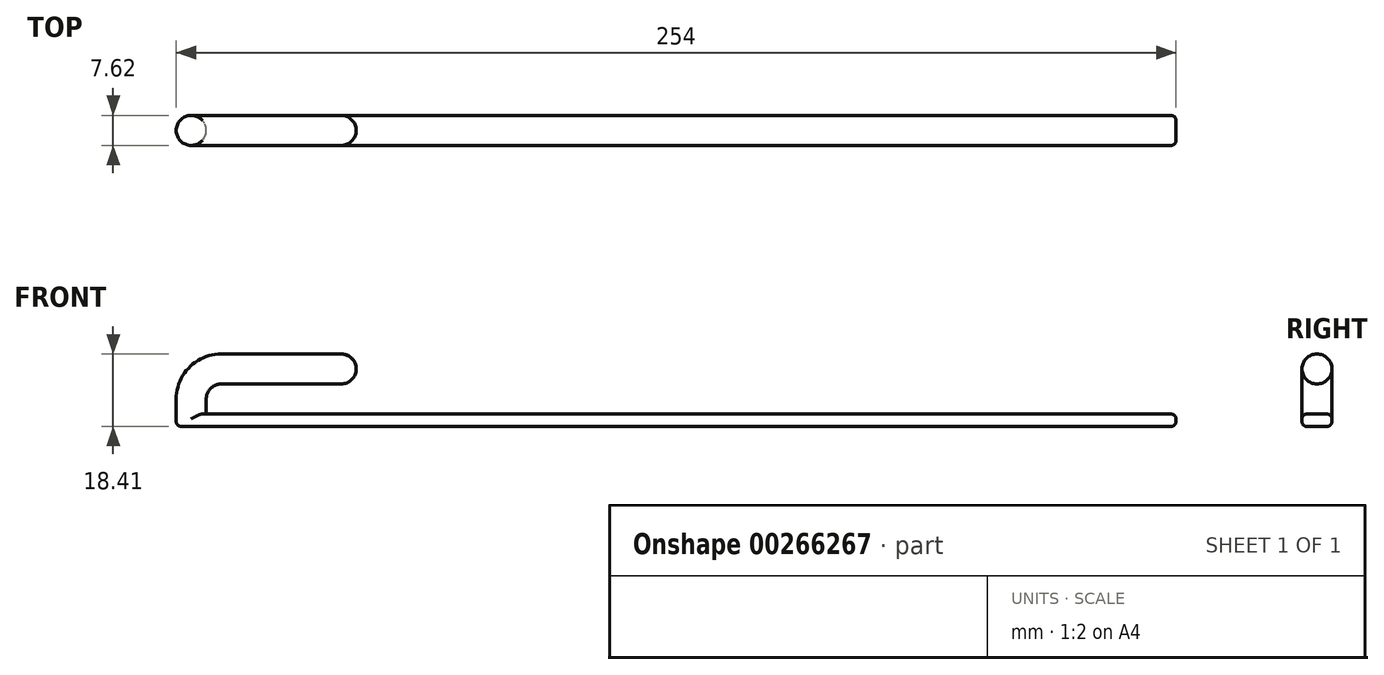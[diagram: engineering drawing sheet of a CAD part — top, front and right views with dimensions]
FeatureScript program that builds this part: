
annotation { "Feature Type Name" : "Feature", "Feature Type Description" : "" }
export const myFeature = defineFeature(function(context is Context, id is Id, definition is map)
    precondition{}
    {
        {
            var Q0;
            Q0=qCreatedBy(makeId("Front.planeOp"),FACE);
            var sketch = newSketch(context, id + "F0", { "sketchPlane" : qUnion([Q0])});
            skLineSegment(sketch, "E0.bottom", {"start": v(-111.6, 37.2) * mm, "end": v(134.77, 37.2) * mm});
            skLineSegment(sketch, "E0.top", {"start": v(-119.23, 34.03) * mm, "end": v(134.77, 34.03) * mm});
            skLineSegment(sketch, "E0.left", {"start": v(-119.23, 39.1) * mm, "end": v(-119.23, 37.2) * mm});
            skLineSegment(sketch, "E0.right", {"start": v(134.77, 37.2) * mm, "end": v(134.77, 34.03) * mm});
            skLineSegment(sketch, "E1.left", {"start": v(-119.23, 34.03) * mm, "end": v(-119.23, 44.82) * mm});
            skLineSegment(sketch, "E1.right", {"start": v(-111.6, 37.2) * mm, "end": v(-111.6, 41.01) * mm});
            skLineSegment(sketch, "E2.bottom", {"start": v(-107.8, 44.82) * mm, "end": v(-73.5, 44.82) * mm});
            skLineSegment(sketch, "E2.top", {"start": v(-107.8, 52.44) * mm, "end": v(-73.5, 52.44) * mm});
            skLineSegment(sketch, "E2.left", {"start": v(-119.23, 41.01) * mm, "end": v(-119.23, 44.82) * mm});
            skLineSegment(sketch, "E2.right", {"start": v(-73.5, 44.82) * mm, "end": v(-73.5, 52.44) * mm});
            skPoint(sketch, "E3.visualSharp", {"position": v(-119.23, 52.44) * mm});
            skArc(sketch, "E3.filletArc", {"start": v(-107.8, 52.44) * mm, "mid": v(-115.88, 49.1) * mm, "end": v(-119.23, 41.01) * mm});
            skPoint(sketch, "E4.visualSharp", {"position": v(-111.6, 44.82) * mm});
            skArc(sketch, "E4.filletArc", {"start": v(-107.8, 44.82) * mm, "mid": v(-110.5, 43.7) * mm, "end": v(-111.6, 41.01) * mm});
            skPoint(sketch, "E5.visualSharp", {"position": v(-111.6, 37.2) * mm});
            skPoint(sketch, "E6.visualSharp", {"position": v(-119.23, 34.03) * mm});
            skSolve(sketch);
        }
        {
            var Q0;
            Q0=makeQuery(id+"F0.imprint","IMPRINT",FACE,{"disambiguationData":[TD([[makeQuery(id+"F0.imprint","IMPRINT",EDGE,{"derivedFrom":sQuery(id+"F0.wireOp",EDGE,"E0.bottom")}),-1.0]])]});
            extrude(context, id + "F1", {"entities" : qUnion([Q0]), "depth" : 7.62 * mm});
        }
        {
            var Q0;
            Q0=makeQuery(id+"F1.opExtrude","CAP_EDGE",EDGE,{"disambiguationData":[OSD([sQuery(id+"F0.wireOp",EDGE,"E2.top")])],"isStart":false});
            var Q1;
            Q1=makeQuery(id+"F1.opExtrude","CAP_EDGE",EDGE,{"disambiguationData":[OSD([sQuery(id+"F0.wireOp",EDGE,"E2.bottom")])],"isStart":false});
            var Q2;
            Q2=makeQuery(id+"F1.opExtrude","CAP_EDGE",EDGE,{"disambiguationData":[OSD([sQuery(id+"F0.wireOp",EDGE,"E2.bottom")])],"isStart":true});
            var Q3;
            Q3=makeQuery(id+"F1.opExtrude","CAP_EDGE",EDGE,{"disambiguationData":[OSD([sQuery(id+"F0.wireOp",EDGE,"E2.top")])],"isStart":true});
            fillet(context, id + "F2", {"entities" : qUnion([Q0, Q1, Q2, Q3]), "radius" : 3.8 * mm, "tangentPropagation" : true, "allowEdgeOverflow" : false});
        }
        {
            var Q0;
            Q0=makeQuery(id+"F1.opExtrude","SWEPT_EDGE",EDGE,{"disambiguationData":[OSD([sQuery(id+"F0.wireOp",EDGE,"E2.top"),sQuery(id+"F0.wireOp",EDGE,"E2.right")])]});
            var Q1;
            Q1=makeQuery(id+"F2.opFillet","BLEND_EDGE",EDGE,{"blendedFrom":[makeQuery(id+"F1.opExtrude","CAP_EDGE",EDGE,{"disambiguationData":[OSD([sQuery(id+"F0.wireOp",EDGE,"E2.top")])],"isStart":true}),makeQuery(id+"F1.opExtrude","SWEPT_FACE",FACE,{"disambiguationData":[OSD([sQuery(id+"F0.wireOp",EDGE,"E2.right")])]})],"blendedInto":[makeQuery(id+"F1.opExtrude","SWEPT_FACE",FACE,{"disambiguationData":[OSD([sQuery(id+"F0.wireOp",EDGE,"E2.right")])]})]});
            var Q2;
            Q2=makeQuery(id+"F1.opExtrude","CAP_EDGE",EDGE,{"disambiguationData":[OSD([sQuery(id+"F0.wireOp",EDGE,"E2.right")])],"isStart":true});
            var Q3;
            Q3=makeQuery(id+"F2.opFillet","BLEND_EDGE",EDGE,{"blendedFrom":[makeQuery(id+"F1.opExtrude","CAP_EDGE",EDGE,{"disambiguationData":[OSD([sQuery(id+"F0.wireOp",EDGE,"E2.bottom")])],"isStart":true}),makeQuery(id+"F1.opExtrude","SWEPT_FACE",FACE,{"disambiguationData":[OSD([sQuery(id+"F0.wireOp",EDGE,"E2.right")])]})],"blendedInto":[makeQuery(id+"F1.opExtrude","SWEPT_FACE",FACE,{"disambiguationData":[OSD([sQuery(id+"F0.wireOp",EDGE,"E2.right")])]})]});
            var Q4;
            Q4=makeQuery(id+"F1.opExtrude","SWEPT_EDGE",EDGE,{"disambiguationData":[OSD([sQuery(id+"F0.wireOp",EDGE,"E2.bottom"),sQuery(id+"F0.wireOp",EDGE,"E2.right")])]});
            var Q5;
            Q5=makeQuery(id+"F2.opFillet","BLEND_EDGE",EDGE,{"blendedFrom":[makeQuery(id+"F1.opExtrude","CAP_EDGE",EDGE,{"disambiguationData":[OSD([sQuery(id+"F0.wireOp",EDGE,"E2.bottom")])],"isStart":false}),makeQuery(id+"F1.opExtrude","SWEPT_FACE",FACE,{"disambiguationData":[OSD([sQuery(id+"F0.wireOp",EDGE,"E2.right")])]})],"blendedInto":[makeQuery(id+"F1.opExtrude","SWEPT_FACE",FACE,{"disambiguationData":[OSD([sQuery(id+"F0.wireOp",EDGE,"E2.right")])]})]});
            var Q6;
            Q6=makeQuery(id+"F2.opFillet","BLEND_EDGE",EDGE,{"blendedFrom":[makeQuery(id+"F1.opExtrude","CAP_EDGE",EDGE,{"disambiguationData":[OSD([sQuery(id+"F0.wireOp",EDGE,"E2.top")])],"isStart":false}),makeQuery(id+"F1.opExtrude","SWEPT_FACE",FACE,{"disambiguationData":[OSD([sQuery(id+"F0.wireOp",EDGE,"E2.right")])]})],"blendedInto":[makeQuery(id+"F1.opExtrude","SWEPT_FACE",FACE,{"disambiguationData":[OSD([sQuery(id+"F0.wireOp",EDGE,"E2.right")])]})]});
            var Q7;
            Q7=makeQuery(id+"F1.opExtrude","CAP_EDGE",EDGE,{"disambiguationData":[OSD([sQuery(id+"F0.wireOp",EDGE,"E2.right")])],"isStart":false});
            fillet(context, id + "F3", {"entities" : qUnion([Q0, Q1, Q2, Q3, Q4, Q5, Q6, Q7]), "radius" : 3.8 * mm, "tangentPropagation" : true, "allowEdgeOverflow" : false});
        }
        {
            var Q0;
            Q0=makeQuery(id+"F1.opExtrude","CAP_EDGE",EDGE,{"disambiguationData":[OSD([sQuery(id+"F0.wireOp",EDGE,"E0.bottom")])],"isStart":false});
            var Q1;
            Q1=makeQuery(id+"F1.opExtrude","CAP_EDGE",EDGE,{"disambiguationData":[OSD([sQuery(id+"F0.wireOp",EDGE,"E0.top")])],"isStart":false});
            var Q2;
            Q2=makeQuery(id+"F1.opExtrude","CAP_EDGE",EDGE,{"disambiguationData":[OSD([sQuery(id+"F0.wireOp",EDGE,"E0.bottom")])],"isStart":true});
            var Q3;
            Q3=makeQuery(id+"F1.opExtrude","CAP_EDGE",EDGE,{"disambiguationData":[OSD([sQuery(id+"F0.wireOp",EDGE,"E0.top")])],"isStart":true});
            fillet(context, id + "F4", {"entities" : qUnion([Q0, Q1, Q2, Q3]), "radius" : 1.27 * mm, "tangentPropagation" : true, "allowEdgeOverflow" : false});
        }
        {
            var Q0;
            Q0=makeQuery(id+"F4.opFillet","BLEND_EDGE",EDGE,{"blendedFrom":[makeQuery(id+"F1.opExtrude","CAP_EDGE",EDGE,{"disambiguationData":[OSD([sQuery(id+"F0.wireOp",EDGE,"E0.bottom")])],"isStart":false}),makeQuery(id+"F1.opExtrude","SWEPT_FACE",FACE,{"disambiguationData":[OSD([sQuery(id+"F0.wireOp",EDGE,"E0.right")])]})],"blendedInto":[makeQuery(id+"F1.opExtrude","SWEPT_FACE",FACE,{"disambiguationData":[OSD([sQuery(id+"F0.wireOp",EDGE,"E0.right")])]})]});
            var Q1;
            Q1=makeQuery(id+"F1.opExtrude","CAP_EDGE",EDGE,{"disambiguationData":[OSD([sQuery(id+"F0.wireOp",EDGE,"E0.right")])],"isStart":false});
            var Q2;
            Q2=makeQuery(id+"F4.opFillet","BLEND_EDGE",EDGE,{"blendedFrom":[makeQuery(id+"F1.opExtrude","CAP_EDGE",EDGE,{"disambiguationData":[OSD([sQuery(id+"F0.wireOp",EDGE,"E0.top")])],"isStart":false}),makeQuery(id+"F1.opExtrude","SWEPT_FACE",FACE,{"disambiguationData":[OSD([sQuery(id+"F0.wireOp",EDGE,"E0.right")])]})],"blendedInto":[makeQuery(id+"F1.opExtrude","SWEPT_FACE",FACE,{"disambiguationData":[OSD([sQuery(id+"F0.wireOp",EDGE,"E0.right")])]})]});
            var Q3;
            Q3=makeQuery(id+"F1.opExtrude","SWEPT_EDGE",EDGE,{"disambiguationData":[OSD([sQuery(id+"F0.wireOp",EDGE,"E0.top"),sQuery(id+"F0.wireOp",EDGE,"E0.right")])]});
            var Q4;
            Q4=makeQuery(id+"F4.opFillet","BLEND_EDGE",EDGE,{"blendedFrom":[makeQuery(id+"F1.opExtrude","CAP_EDGE",EDGE,{"disambiguationData":[OSD([sQuery(id+"F0.wireOp",EDGE,"E0.top")])],"isStart":true}),makeQuery(id+"F1.opExtrude","SWEPT_FACE",FACE,{"disambiguationData":[OSD([sQuery(id+"F0.wireOp",EDGE,"E0.right")])]})],"blendedInto":[makeQuery(id+"F1.opExtrude","SWEPT_FACE",FACE,{"disambiguationData":[OSD([sQuery(id+"F0.wireOp",EDGE,"E0.right")])]})]});
            var Q5;
            Q5=makeQuery(id+"F1.opExtrude","CAP_EDGE",EDGE,{"disambiguationData":[OSD([sQuery(id+"F0.wireOp",EDGE,"E0.right")])],"isStart":true});
            var Q6;
            Q6=makeQuery(id+"F1.opExtrude","SWEPT_EDGE",EDGE,{"disambiguationData":[OSD([sQuery(id+"F0.wireOp",EDGE,"E0.bottom"),sQuery(id+"F0.wireOp",EDGE,"E0.right")])]});
            var Q7;
            Q7=makeQuery(id+"F4.opFillet","BLEND_EDGE",EDGE,{"blendedFrom":[makeQuery(id+"F1.opExtrude","CAP_EDGE",EDGE,{"disambiguationData":[OSD([sQuery(id+"F0.wireOp",EDGE,"E0.bottom")])],"isStart":true}),makeQuery(id+"F1.opExtrude","SWEPT_FACE",FACE,{"disambiguationData":[OSD([sQuery(id+"F0.wireOp",EDGE,"E0.right")])]})],"blendedInto":[makeQuery(id+"F1.opExtrude","SWEPT_FACE",FACE,{"disambiguationData":[OSD([sQuery(id+"F0.wireOp",EDGE,"E0.right")])]})]});
            fillet(context, id + "F5", {"entities" : qUnion([Q0, Q1, Q2, Q3, Q4, Q5, Q6, Q7]), "radius" : 1.27 * mm, "tangentPropagation" : true, "allowEdgeOverflow" : false});
        }
    });
